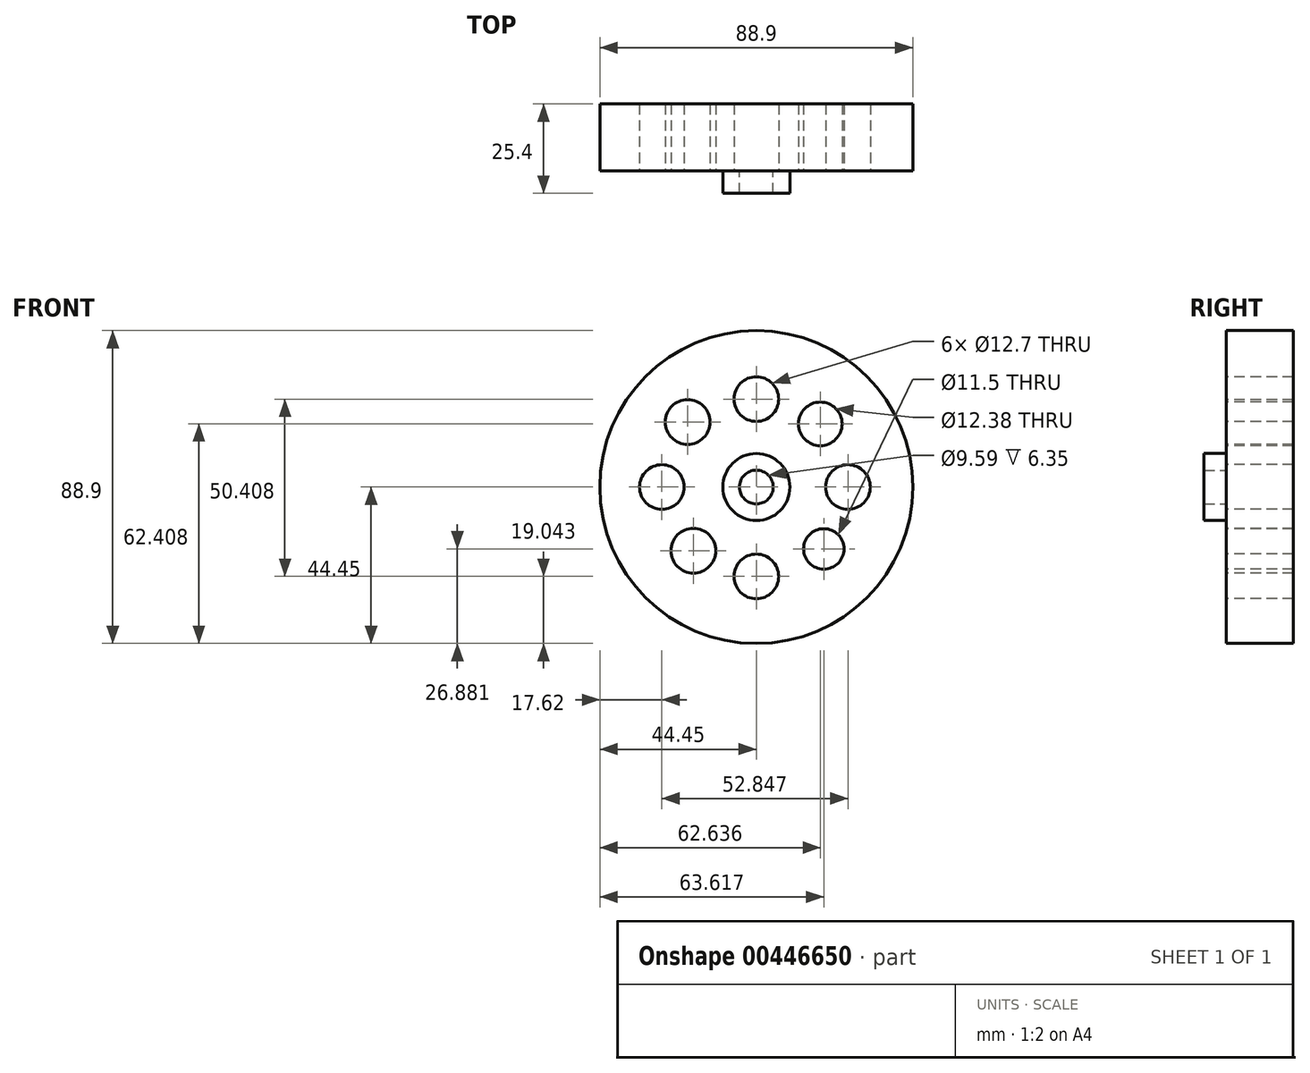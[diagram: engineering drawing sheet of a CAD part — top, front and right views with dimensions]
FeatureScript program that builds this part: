
annotation { "Feature Type Name" : "Feature", "Feature Type Description" : "" }
export const myFeature = defineFeature(function(context is Context, id is Id, definition is map)
    precondition{}
    {
        {
            var Q0;
            Q0=qCreatedBy(makeId("Front.planeOp"),FACE);
            var sketch = newSketch(context, id + "F0", { "sketchPlane" : qUnion([Q0])});
            skCircle(sketch, "E0", {"center": v(0, 0) * mm, "radius": 44.45 * mm});
            skSolve(sketch);
        }
        {
            var Q0;
            Q0 = qSketchRegion(id + "F0", true);
            extrude(context, id + "F1", {"entities" : qUnion([Q0]), "depth" : 19.05 * mm});
        }
        {
            var Q0;
            Q0=makeQuery(id+"F1.opExtrude","CAP_FACE",FACE,{"disambiguationData":[OSD([sQuery(id+"F0.wireOp",EDGE,"E0")])],"isStart":false});
            var sketch = newSketch(context, id + "F2", { "sketchPlane" : qUnion([Q0])});
            skCircle(sketch, "E1", {"center": v(0, 25) * mm, "radius": 6.35 * mm});
            skCircle(sketch, "E2", {"center": v(0, -25.4) * mm, "radius": 6.35 * mm});
            skCircle(sketch, "E3", {"center": v(26.02, 0) * mm, "radius": 6.35 * mm});
            skCircle(sketch, "E4", {"center": v(-26.83, 0) * mm, "radius": 6.35 * mm});
            skCircle(sketch, "E5", {"center": v(18.19, 17.96) * mm, "radius": 6.2 * mm});
            skCircle(sketch, "E6", {"center": v(19.17, -17.57) * mm, "radius": 5.75 * mm});
            skCircle(sketch, "E7", {"center": v(-17.89, -18.1) * mm, "radius": 6.35 * mm});
            skCircle(sketch, "E8", {"center": v(-19.51, 18.5) * mm, "radius": 6.35 * mm});
            skSolve(sketch);
        }
        {
            var Q0;
            Q0 = qSketchRegion(id + "F2", true);
            extrude(context, id + "F3", {"entities" : qUnion([Q0]), "operationType" : NewBodyOperationType.REMOVE, "oppositeDirection" : true, "depth" : 25.4 * mm});
        }
        {
            var Q0;
            Q0=makeQuery(id+"F1.opExtrude","CAP_FACE",FACE,{"disambiguationData":[OSD([sQuery(id+"F0.wireOp",EDGE,"E0")])],"isStart":false});
            var sketch = newSketch(context, id + "F4", { "sketchPlane" : qUnion([Q0])});
            skCircle(sketch, "E9", {"center": v(0, 0) * mm, "radius": 9.53 * mm});
            skCircle(sketch, "E10", {"center": v(0, 0) * mm, "radius": 4.8 * mm});
            skSolve(sketch);
        }
        {
            var Q0;
            Q0=makeQuery(id+"F4.imprint","IMPRINT",FACE,{"disambiguationData":[TD([[makeQuery(id+"F4.imprint","IMPRINT",EDGE,{"derivedFrom":sQuery(id+"F4.wireOp",EDGE,"E9")}),1.0]])]});
            extrude(context, id + "F5", {"entities" : qUnion([Q0]), "operationType" : NewBodyOperationType.ADD, "depth" : 6.35 * mm});
        }
    });
